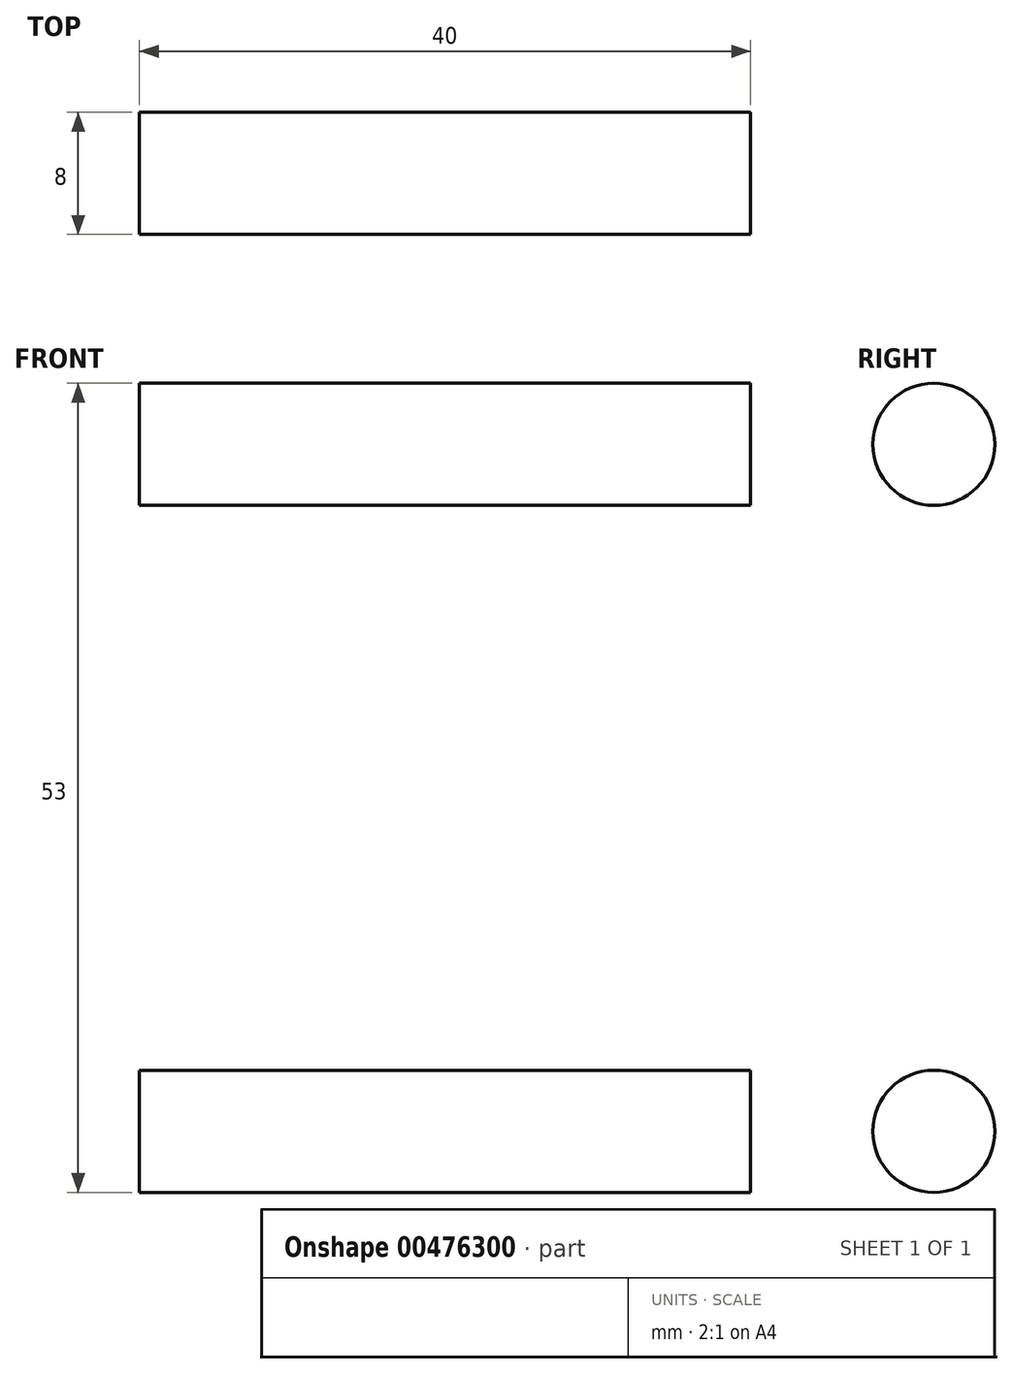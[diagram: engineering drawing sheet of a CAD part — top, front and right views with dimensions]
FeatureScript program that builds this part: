
annotation { "Feature Type Name" : "Feature", "Feature Type Description" : "" }
export const myFeature = defineFeature(function(context is Context, id is Id, definition is map)
    precondition{}
    {
        {
            var Q0;
            Q0=qCreatedBy(makeId("Right.planeOp"),FACE);
            var sketch = newSketch(context, id + "F0", { "sketchPlane" : qUnion([Q0])});
            skCircle(sketch, "E0", {"center": v(0, 22.5) * mm, "radius": 4 * mm});
            skCircle(sketch, "E1", {"center": v(0, -22.5) * mm, "radius": 4 * mm});
            skSolve(sketch);
        }
        {
            var Q0;
            Q0=makeQuery(id+"F0.imprint","IMPRINT",FACE,{"disambiguationData":[TD([[makeQuery(id+"F0.imprint","IMPRINT",EDGE,{"derivedFrom":sQuery(id+"F0.wireOp",EDGE,"E0")}),1.0]])]});
            var Q1;
            Q1=makeQuery(id+"F0.imprint","IMPRINT",FACE,{"disambiguationData":[TD([[makeQuery(id+"F0.imprint","IMPRINT",EDGE,{"derivedFrom":sQuery(id+"F0.wireOp",EDGE,"E1")}),1.0]])]});
            extrude(context, id + "F1", {"entities" : qUnion([Q0, Q1]), "depth" : 20 * mm, "hasSecondDirection" : true, "secondDirectionOppositeDirection" : true, "secondDirectionDepth" : 20 * mm});
        }
        {
            var Q0;
            Q0=qCreatedBy(makeId("Front.planeOp"),FACE);
            cPlane(context, id + "F2", {"entities" : qUnion([Q0]), "cplaneType" : CPlaneType.OFFSET, "offset" : 4 * mm, "width" : 150 * mm, "height" : 150 * mm});
        }
    });
